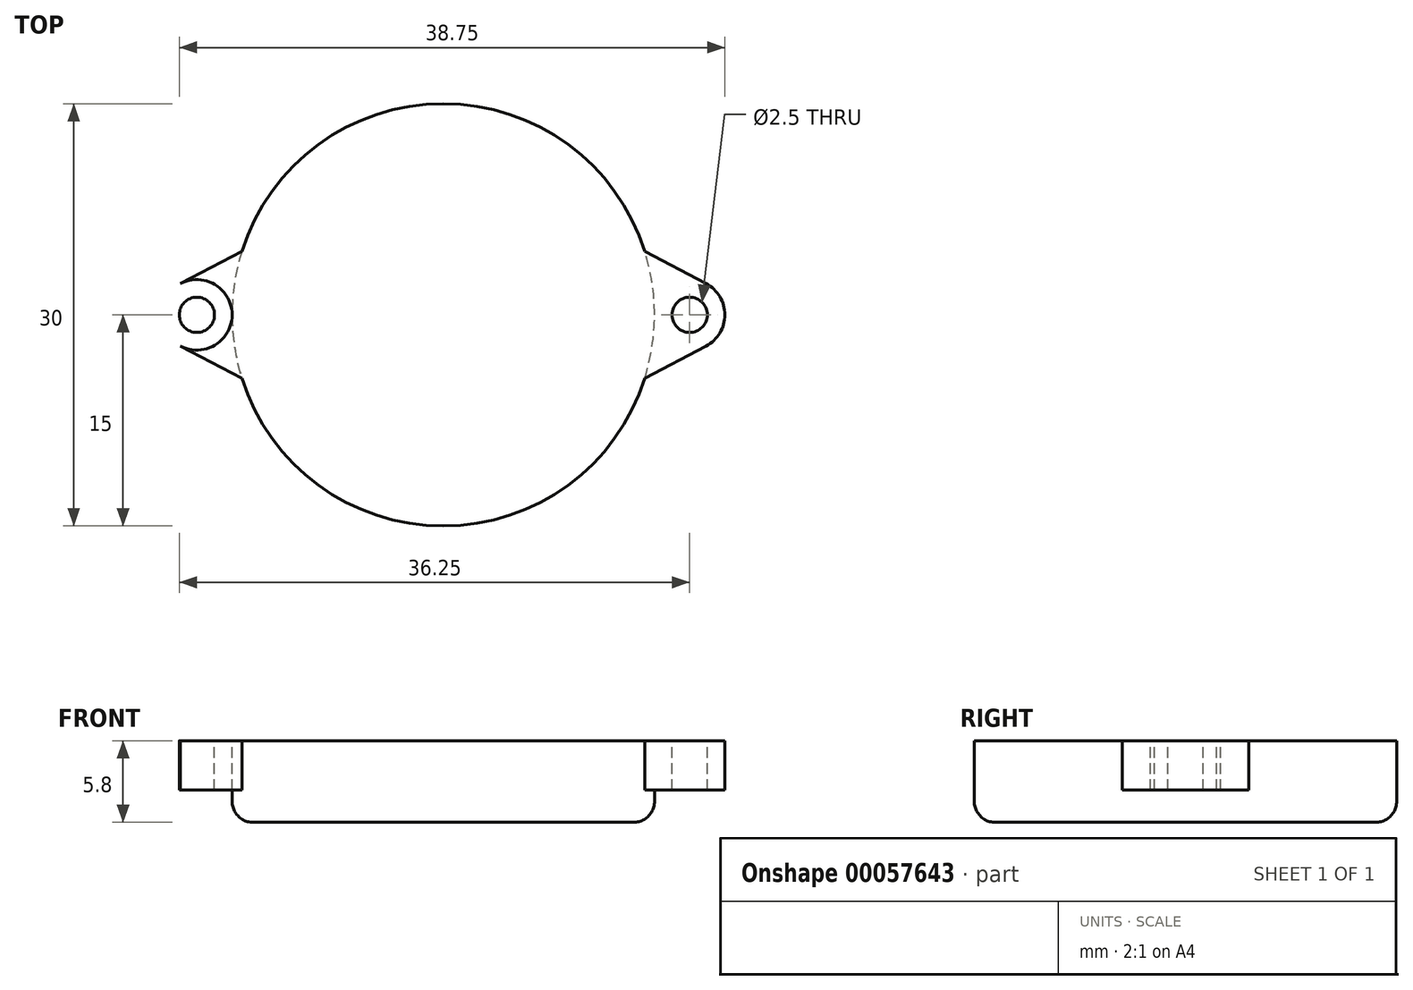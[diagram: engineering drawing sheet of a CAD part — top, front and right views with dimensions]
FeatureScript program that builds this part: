
annotation { "Feature Type Name" : "Feature", "Feature Type Description" : "" }
export const myFeature = defineFeature(function(context is Context, id is Id, definition is map)
    precondition{}
    {
        {
            var Q0;
            Q0=qCreatedBy(makeId("Top.planeOp"),FACE);
            var sketch = newSketch(context, id + "F0", { "sketchPlane" : qUnion([Q0])});
            skCircle(sketch, "E0", {"center": v(0, 0) * mm, "radius": 15 * mm});
            skPoint(sketch, "E1", {"position": v(17.5, 0) * mm});
            skPoint(sketch, "E2.MirrorP", {"position": v(-17.5, 0) * mm});
            skCircle(sketch, "E3", {"center": v(17.5, 0) * mm, "radius": 1.25 * mm});
            skPoint(sketch, "E4", {"position": v(20, 0) * mm});
            skCircle(sketch, "E5", {"center": v(17.5, 0) * mm, "radius": 2.5 * mm});
            skLineSegment(sketch, "E6", {"start": v(14.3, 4.5) * mm, "end": v(18.66, 2.21) * mm});
            skLineSegment(sketch, "E7.MirrorCS", {"start": v(14.3, -4.5) * mm, "end": v(18.66, -2.21) * mm});
            skCircle(sketch, "E8.MirrorC", {"center": v(-17.5, 0) * mm, "radius": 1.25 * mm});
            skCircle(sketch, "E9.MirrorC", {"center": v(-17.5, 0) * mm, "radius": 2.5 * mm});
            skLineSegment(sketch, "E10.MirrorCS", {"start": v(-14.3, 4.5) * mm, "end": v(-18.66, 2.21) * mm});
            skLineSegment(sketch, "E11.MirrorCS", {"start": v(-14.3, -4.5) * mm, "end": v(-18.66, -2.21) * mm});
            skSolve(sketch);
        }
        {
            var Q0;
            {var subQ0=sQuery(id+"F0.wireOp",EDGE,"E0");var subQ4=makeQuery(id+"F0.imprint","INTERSECT",VERTEX,{"derivedFrom":[subQ0,sQuery(id+"F0.wireOp",EDGE,"E6")]});Q0=makeQuery(id+"F0.imprint","IMPRINT",FACE,{"disambiguationData":[TD([[makeQuery(id+"F0.imprint","IMPRINT",EDGE,{"disambiguationData":[TD([[subQ4,1.0]])],"derivedFrom":subQ0}),1.0]])]});}
            extrude(context, id + "F1", {"entities" : qUnion([Q0]), "oppositeDirection" : true, "depth" : 5.8 * mm});
        }
        {
            var Q0;
            Q0=makeQuery(id+"F0.imprint","IMPRINT",FACE,{"disambiguationData":[TD([[makeQuery(id+"F0.imprint","IMPRINT",EDGE,{"derivedFrom":sQuery(id+"F0.wireOp",EDGE,"E8.MirrorC")}),1.0]])]});
            var Q1;
            {var subQ0=sQuery(id+"F0.wireOp",EDGE,"E11.MirrorCS");Q1=makeQuery(id+"F0.imprint","IMPRINT",FACE,{"disambiguationData":[TD([[makeQuery(id+"F0.imprint","IMPRINT",EDGE,{"derivedFrom":subQ0}),-1.0]])]});}
            var Q2;
            {var subQ0=sQuery(id+"F0.wireOp",EDGE,"E10.MirrorCS");Q2=makeQuery(id+"F0.imprint","IMPRINT",FACE,{"disambiguationData":[TD([[makeQuery(id+"F0.imprint","IMPRINT",EDGE,{"derivedFrom":subQ0}),1.0]])]});}
            var Q3;
            {var subQ0=sQuery(id+"F0.wireOp",EDGE,"E6");Q3=makeQuery(id+"F0.imprint","IMPRINT",FACE,{"disambiguationData":[TD([[makeQuery(id+"F0.imprint","IMPRINT",EDGE,{"derivedFrom":subQ0}),-1.0]])]});}
            var Q4;
            Q4=makeQuery(id+"F0.imprint","IMPRINT",FACE,{"disambiguationData":[TD([[makeQuery(id+"F0.imprint","IMPRINT",EDGE,{"derivedFrom":sQuery(id+"F0.wireOp",EDGE,"E3")}),-1.0]])]});
            var Q5;
            {var subQ0=sQuery(id+"F0.wireOp",EDGE,"E7.MirrorCS");Q5=makeQuery(id+"F0.imprint","IMPRINT",FACE,{"disambiguationData":[TD([[makeQuery(id+"F0.imprint","IMPRINT",EDGE,{"derivedFrom":subQ0}),1.0]])]});}
            extrude(context, id + "F2", {"entities" : qUnion([Q0, Q1, Q2, Q3, Q4, Q5]), "operationType" : NewBodyOperationType.ADD, "oppositeDirection" : true, "depth" : 3.5 * mm});
        }
        {
            var Q0;
            Q0=makeQuery(id+"F1.opExtrude","CAP_EDGE",EDGE,{"disambiguationData":[OSD([sQuery(id+"F0.wireOp",EDGE,"E0")])],"isStart":false});
            fillet(context, id + "F3", {"entities" : qUnion([Q0]), "radius" : 1.5 * mm, "tangentPropagation" : true, "allowEdgeOverflow" : false});
        }
    });
